# Revit family: Curtain_Door-Single-CRL-Balancer_Series-Aluminum-Full_Frame
name_source: partatom
category: Doors
revit_build: Autodesk Revit Architecture 2015 (Build: 20140606_1530(x64)
units: mm (PartAtom-declared; Revit-internal decimal feet)

## types (1)
- SEE CATALOG
    Assembly Code = B2030110
    Bottom Rail Height = 0' - 10"
    Construction Note = Maximum Size for Balancer Series is 48" Wide x 108" High (1219 x 2743 mm)
    Description = Balancer Series Doors
    Function = Exterior
    Glass = Glass - C.R. Laurence - Clear Glazing
    Glass Thickness = 0' - 1"
    Hardware Finish = Metal - C.R. Laurence - Clear Anodized – Aluminum
    Hinge Arm Length = 0' - 7 1/8"
    Hinge Divide Calc = 0' - 10 1/2"
    Long Arm = No
    Manufacturer = C.R. Laurence - U.S. Aluminum
    Material Note = Custom paint is available please contact vendor for more information
    Model = Balancer Series
    Panel = Metal - C.R. Laurence - Clear Anodized – Aluminum
    Panel Arm Length = 1' - 0 1/2"
    Panel Thickness = 0' - 1 7/8"
    Product Documentation Link = http://www.crl-arch.com
    Product Page URL = http://www.crl-arch.com
    Product data url = https://bimobject.com
    Short Arm = Yes
    Show Hardware = Yes
    Stile Width = 0' - 4 1/4"
    Thickness = 0' - 1 7/8"
    Top Rail Height = 0' - 3 1/4"
    URL = http://www.crl-arch.com

## geometry (parser evidence)
native form markers: Blend x4, Sweep x16
no freeform markers — native parametric forms only
